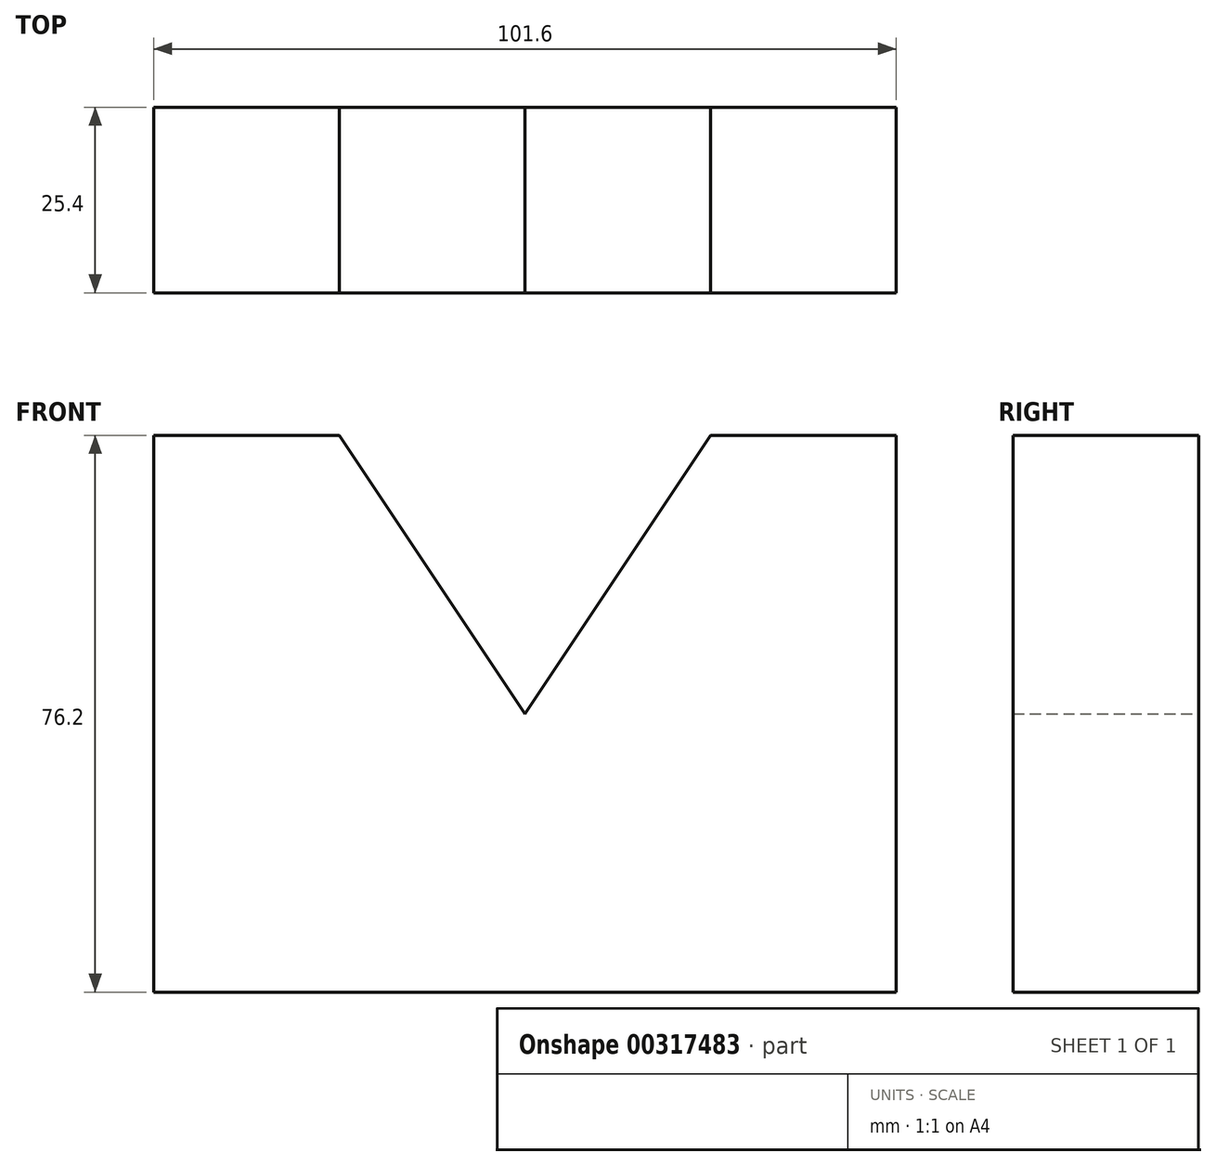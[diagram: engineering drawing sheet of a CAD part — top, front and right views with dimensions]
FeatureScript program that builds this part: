
annotation { "Feature Type Name" : "Feature", "Feature Type Description" : "" }
export const myFeature = defineFeature(function(context is Context, id is Id, definition is map)
    precondition{}
    {
        {
            var Q0;
            Q0=qCreatedBy(makeId("Front.planeOp"),FACE);
            var sketch = newSketch(context, id + "F0", { "sketchPlane" : qUnion([Q0])});
            skLineSegment(sketch, "E0", {"start": v(-43.85, -62.12) * mm, "end": v(57.75, -62.12) * mm});
            skLineSegment(sketch, "E1", {"start": v(57.75, -62.12) * mm, "end": v(57.75, 14.08) * mm});
            skLineSegment(sketch, "E2", {"start": v(57.75, 14.08) * mm, "end": v(32.35, 14.08) * mm});
            skLineSegment(sketch, "E3", {"start": v(-43.85, -62.12) * mm, "end": v(-43.85, 14.08) * mm});
            skLineSegment(sketch, "E4", {"start": v(-43.85, 14.08) * mm, "end": v(-18.45, 14.08) * mm});
            skLineSegment(sketch, "E5", {"start": v(6.95, -24.02) * mm, "end": v(-18.45, 14.08) * mm});
            skLineSegment(sketch, "E6", {"start": v(6.95, -24.02) * mm, "end": v(32.35, 14.08) * mm});
            skSolve(sketch);
        }
        {
            var Q0;
            Q0 = qSketchRegion(id + "F0", true);
            extrude(context, id + "F1", {"entities" : qUnion([Q0]), "depth" : 25.4 * mm});
        }
    });
